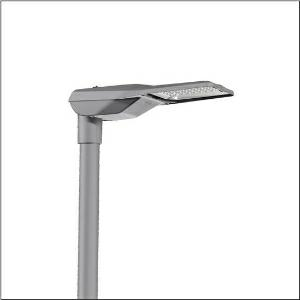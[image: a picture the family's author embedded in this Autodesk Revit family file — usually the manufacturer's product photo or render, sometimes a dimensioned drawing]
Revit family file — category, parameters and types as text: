
# Revit family: streetlight_sl_21_mini___p1_0a_5xe2a43s08gb_f3ee
name_source: partatom
category: Lighting Fixtures
units: mm (PartAtom-declared; Revit-internal decimal feet)

## family parameters
Cut with Voids When Loaded = No
Host = Face
Light Source = No
Part Type = Normal
Room Calculation Point = No
Round Connector Dimension = Use Diameter
Shared = No

## types (1)
- --- (1 x LED, 6180 lm, 40.4 W, 4000K)
    Apparent Load = 40 VA
    CIE Flux Codes = 21 50 90 100 100
    Color Rendering = 70
    Color Temperature = 4000K
    Default Elevation = 1800 mm
    Description = Streetlight SL 21 mini, mast luminaire, primary light control with lens, of PMMA, primary optical cover: cover, of toughened safety glass, transparent, light distribution: P1.0a, light emission: direct distribution, primary light characteristic: asymmetric, installation type: side-entry, post-top, LED, High Power LED, rated luminous flux: 6.180lm, luminous efficacy: 153lm/W, light colour: 740, colour temperature: 4000K, control gear: D4i, control: overheat protection, constant luminous flux control, time-dependent luminous flux control, flexible luminous flux parameterisation, pre-setting: logarithmic dimming characteristic, mains connection: 220..240V, AC, 50/60Hz, start of lifetime: 40W, end of service life: 41W, reduction: 19W, luminaire housing, of diecast aluminium, powder-coated, SITECO metallic grey (DB 702S), corrosivity category C5 high according to DIN EN ISO 12944, please order mast flange separately, inclination adjustable: 0°, 5°, 10°, 15°, sealing non-destructively replaceable, multi-level sealing system, length: 628mm, width: 235mm, height: 110mm, mast flange for spigot size: 42mm (side-entry): 5XC10008XM4, 60/48mm (side-entry/post-top): 5XC10108XM2, 76/60mm (side-entry/post-top): 5XC10108XM1, mounting height: 4..8m, Smart Interface above, protection rating (complete): IP66, insulation class (complete): insulation class II (safety insulation), certification: CE, ENEC, ENEC+, VDE, impact resistance: IK10, permissible operating ambient temperature for outdoor applications: -40..+50°C, standard-compliant lighting for roads and squares, packaging unit: 1 piece

Light Distribution: P1.0a
    Height = 110 mm
    Lamp = 1 x LED
    Lamp Light Flux = 6180 lm
    Lamp Power = 40.4 W
    Lamp count = 1
    Length = 625 mm
    Luminous efficacy = 153 lm/W
    Manufacturer = Siteco
    ModVariant = No
    Model = 5XE2A43S08GB
    Number of Poles = 1
    OnlyDefault = Yes
    Power Factor = 1
    Product Name = Streetlight SL 21 mini | P1.0a
    Product group = mast luminaire | pylon top
    ProductGroupID = 6100
    Protection Class = Protection class II
    Protection Degree = IP 66
    RLX_Detail_Level = 1
    RLX_Emergency_Light_Flux = 0 lm
    RLX_Emergency_Type = 0
    RLX_Emergency_Type_DB = No
    RlxData = <blob elided: 37325 chars, md5=f00a0a7d>
    Socket = socket
    Standby Power = 0 W
    System Light Flux = 6180 lm
    System Power = 40 W
    Type Comments = factory setting: luminous flux: 100 % | dim-lin: 254 | 812 mA
    Type Image = l_1003515.jpg
    URL = http://relux.com
    VarID = @adj_184127
    Voltage = 0 V
    Weight = 0.00 kg
    Width = 234 mm

## geometry (parser evidence)
native form markers: Blend x4, Sweep x10
no freeform markers — native parametric forms only
